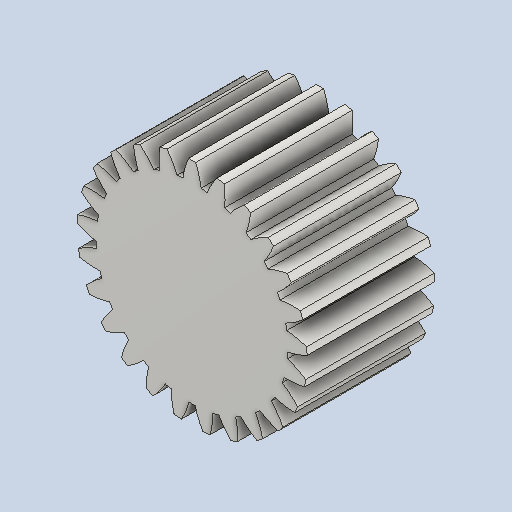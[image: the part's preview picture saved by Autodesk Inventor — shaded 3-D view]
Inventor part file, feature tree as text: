
AUTODESK INVENTOR PART (.ipt)
format: ipt  version: 2024 (Build 280153000, 153)  size: 277,504 bytes
history: native  units: mm (DEFAULTED — no unit token found)
features: plane x3, other x3, extrude x1, sketch x1
ambient origin geometry x8: Origin, YZ Plane, XZ Plane, XY Plane, X Axis, Y Axis, Z Axis, Center Point
bodies: Solid1 (feature_tree)
feature tree (8):
  extrude  "Extrusion1"  Depth=30.0mm TaperAngle=0.0deg
  plane  "Work Plane2"
  plane  "Work Plane8"
  plane  "Work Plane9"
  other  "Spur Gear"
  sketch  "Sketch1"  dims[d0=54.0mm d1=30.0mm d2=0.0mm d3=50.0mm d4=10.0mm d5=0.0mm d16=35.0mm d17=0.0mm d34=1.256637mm d39=0.0mm d41=0.0mm d43=35.0mm d46=35.0mm d47=0.0mm d48=0.0mm]
  other  "Srf1"
  other  "Pitch Diameter"
